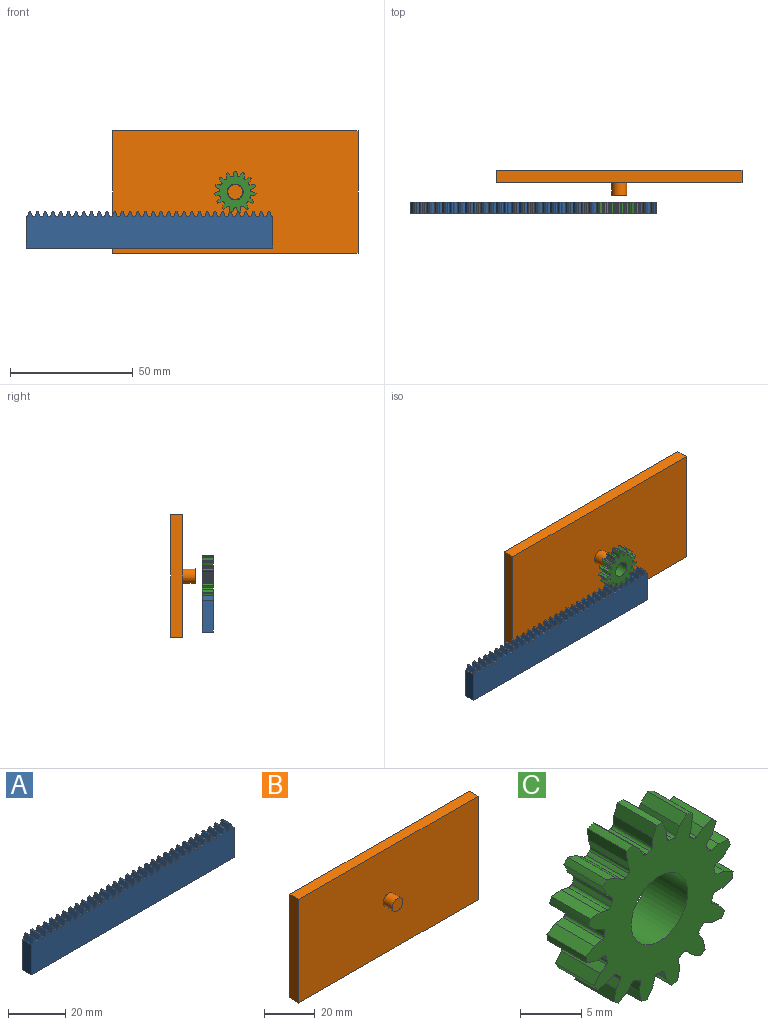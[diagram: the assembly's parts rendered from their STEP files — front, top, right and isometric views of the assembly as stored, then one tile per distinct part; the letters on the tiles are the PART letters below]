
ASSEMBLY  parts=3 mates=2
PART A: 134 faces, bbox 100.5x4.5x15 mm
  f0: plane 4.5x0.53mm, normal (0,0,1), area 2.4mm2, adj f1,f131,f132,f133
  f1: plane 4.5x2.1mm, normal (0.94,0,0.34), area 10.1mm2, adj f0,f2,f132,f133
  f2: plane 4.5x0.55mm, normal (0,0,1), area 2.5mm2, adj f1,f3,f132,f133
  f3: plane 4.5x2.1mm, normal (-0.94,0,0.34), area 10.1mm2, adj f2,f4,f132,f133
  f4: plane 4.5x1.07mm, normal (0,0,1), area 4.8mm2, adj f3,f5,f132,f133
  f5: plane 4.5x2.1mm, normal (0.94,0,0.34), area 10.1mm2, adj f4,f6,f132,f133
  f6: plane 4.5x0.55mm, normal (0,0,1), area 2.5mm2, adj f5,f7,f132,f133
  f7: plane 4.5x2.1mm, normal (-0.94,0,0.34), area 10.1mm2, adj f6,f8,f132,f133
  f8: plane 4.5x1.07mm, normal (0,0,1), area 4.8mm2, adj f7,f9,f132,f133
  f9: plane 4.5x2.1mm, normal (0.94,0,0.34), area 10.1mm2, adj f8,f10,f132,f133
  f10: plane 4.5x0.55mm, normal (0,0,1), area 2.5mm2, adj f9,f11,f132,f133
  f11: plane 4.5x2.1mm, normal (-0.94,0,0.34), area 10.1mm2, adj f10,f12,f132,f133
  f12: plane 4.5x1.07mm, normal (0,0,1), area 4.8mm2, adj f11,f13,f132,f133
  f13: plane 4.5x2.1mm, normal (0.94,0,0.34), area 10.1mm2, adj f12,f14,f132,f133
  f14: plane 4.5x0.55mm, normal (0,0,1), area 2.5mm2, adj f13,f15,f132,f133
  f15: plane 4.5x2.1mm, normal (-0.94,0,0.34), area 10.1mm2, adj f14,f16,f132,f133
  f16: plane 4.5x1.07mm, normal (0,0,1), area 4.8mm2, adj f15,f17,f132,f133
  f17: plane 4.5x2.1mm, normal (0.94,0,0.34), area 10.1mm2, adj f16,f18,f132,f133
  f18: plane 4.5x0.55mm, normal (0,0,1), area 2.5mm2, adj f17,f19,f132,f133
  f19: plane 4.5x2.1mm, normal (-0.94,0,0.34), area 10.1mm2, adj f18,f20,f132,f133
  f20: plane 4.5x1.07mm, normal (0,0,1), area 4.8mm2, adj f19,f21,f132,f133
  f21: plane 4.5x2.1mm, normal (0.94,0,0.34), area 10.1mm2, adj f20,f22,f132,f133
  f22: plane 4.5x0.55mm, normal (0,0,1), area 2.5mm2, adj f21,f23,f132,f133
  f23: plane 4.5x2.1mm, normal (-0.94,0,0.34), area 10.1mm2, adj f22,f24,f132,f133
  f24: plane 4.5x1.07mm, normal (0,0,1), area 4.8mm2, adj f23,f25,f132,f133
  f25: plane 4.5x2.1mm, normal (0.94,0,0.34), area 10.1mm2, adj f24,f26,f132,f133
  f26: plane 4.5x0.55mm, normal (0,0,1), area 2.5mm2, adj f25,f27,f132,f133
  f27: plane 4.5x2.1mm, normal (-0.94,0,0.34), area 10.1mm2, adj f26,f28,f132,f133
  f28: plane 4.5x1.07mm, normal (0,0,1), area 4.8mm2, adj f27,f29,f132,f133
  f29: plane 4.5x2.1mm, normal (0.94,0,0.34), area 10.1mm2, adj f28,f30,f132,f133
  f30: plane 4.5x0.55mm, normal (0,0,1), area 2.5mm2, adj f29,f31,f132,f133
  f31: plane 4.5x2.1mm, normal (-0.94,0,0.34), area 10.1mm2, adj f30,f32,f132,f133
  f32: plane 4.5x1.07mm, normal (0,0,1), area 4.8mm2, adj f31,f33,f132,f133
  f33: plane 4.5x2.1mm, normal (0.94,0,0.34), area 10.1mm2, adj f32,f34,f132,f133
  f34: plane 4.5x0.55mm, normal (0,0,1), area 2.5mm2, adj f33,f35,f132,f133
  f35: plane 4.5x2.1mm, normal (-0.94,0,0.34), area 10.1mm2, adj f34,f36,f132,f133
  f36: plane 4.5x1.07mm, normal (0,0,1), area 4.8mm2, adj f35,f37,f132,f133
  f37: plane 4.5x2.1mm, normal (0.94,0,0.34), area 10.1mm2, adj f36,f38,f132,f133
  f38: plane 4.5x0.55mm, normal (0,0,1), area 2.5mm2, adj f37,f39,f132,f133
  f39: plane 4.5x2.1mm, normal (-0.94,0,0.34), area 10.1mm2, adj f38,f40,f132,f133
  f40: plane 4.5x1.07mm, normal (0,0,1), area 4.8mm2, adj f39,f41,f132,f133
  f41: plane 4.5x2.1mm, normal (0.94,0,0.34), area 10.1mm2, adj f40,f42,f132,f133
  f42: plane 4.5x0.55mm, normal (0,0,1), area 2.5mm2, adj f41,f43,f132,f133
  f43: plane 4.5x2.1mm, normal (-0.94,0,0.34), area 10.1mm2, adj f42,f44,f132,f133
  f44: plane 4.5x1.07mm, normal (0,0,1), area 4.8mm2, adj f43,f45,f132,f133
  f45: plane 4.5x2.1mm, normal (0.94,0,0.34), area 10.1mm2, adj f44,f46,f132,f133
  f46: plane 4.5x0.55mm, normal (0,0,1), area 2.5mm2, adj f45,f47,f132,f133
  f47: plane 4.5x2.1mm, normal (-0.94,0,0.34), area 10.1mm2, adj f46,f48,f132,f133
  f48: plane 4.5x1.07mm, normal (0,0,1), area 4.8mm2, adj f47,f49,f132,f133
  f49: plane 4.5x2.1mm, normal (0.94,0,0.34), area 10.1mm2, adj f48,f50,f132,f133
  f50: plane 4.5x0.55mm, normal (0,0,1), area 2.5mm2, adj f49,f51,f132,f133
  f51: plane 4.5x2.1mm, normal (-0.94,0,0.34), area 10.1mm2, adj f50,f52,f132,f133
  f52: plane 4.5x1.07mm, normal (0,0,1), area 4.8mm2, adj f51,f53,f132,f133
  f53: plane 4.5x2.1mm, normal (0.94,0,0.34), area 10.1mm2, adj f52,f54,f132,f133
  f54: plane 4.5x0.55mm, normal (0,0,1), area 2.5mm2, adj f53,f55,f132,f133
  f55: plane 4.5x2.1mm, normal (-0.94,0,0.34), area 10.1mm2, adj f54,f56,f132,f133
  f56: plane 4.5x1.07mm, normal (0,0,1), area 4.8mm2, adj f55,f57,f132,f133
  f57: plane 4.5x2.1mm, normal (0.94,0,0.34), area 10.1mm2, adj f56,f58,f132,f133
  f58: plane 4.5x0.55mm, normal (0,0,1), area 2.5mm2, adj f57,f59,f132,f133
  f59: plane 4.5x2.1mm, normal (-0.94,0,0.34), area 10.1mm2, adj f58,f60,f132,f133
  f60: plane 4.5x1.07mm, normal (0,0,1), area 4.8mm2, adj f59,f61,f132,f133
  f61: plane 4.5x2.1mm, normal (0.94,0,0.34), area 10.1mm2, adj f60,f62,f132,f133
  f62: plane 4.5x0.55mm, normal (0,0,1), area 2.5mm2, adj f61,f63,f132,f133
  f63: plane 4.5x2.1mm, normal (-0.94,0,0.34), area 10.1mm2, adj f62,f64,f132,f133
  f64: plane 4.5x1.07mm, normal (0,0,1), area 4.8mm2, adj f63,f65,f132,f133
  f65: plane 4.5x2.1mm, normal (0.94,0,0.34), area 10.1mm2, adj f64,f66,f132,f133
  f66: plane 4.5x0.55mm, normal (0,0,1), area 2.5mm2, adj f65,f67,f132,f133
  f67: plane 4.5x2.1mm, normal (-0.94,0,0.34), area 10.1mm2, adj f66,f68,f132,f133
  f68: plane 4.5x1.07mm, normal (0,0,1), area 4.8mm2, adj f67,f69,f132,f133
  f69: plane 4.5x2.1mm, normal (0.94,0,0.34), area 10.1mm2, adj f68,f70,f132,f133
  f70: plane 4.5x0.55mm, normal (0,0,1), area 2.5mm2, adj f69,f71,f132,f133
  f71: plane 4.5x2.1mm, normal (-0.94,0,0.34), area 10.1mm2, adj f70,f72,f132,f133
  f72: plane 4.5x1.07mm, normal (0,0,1), area 4.8mm2, adj f71,f73,f132,f133
  f73: plane 4.5x2.1mm, normal (0.94,0,0.34), area 10.1mm2, adj f72,f74,f132,f133
  f74: plane 4.5x0.55mm, normal (0,0,1), area 2.5mm2, adj f73,f75,f132,f133
  f75: plane 4.5x2.1mm, normal (-0.94,0,0.34), area 10.1mm2, adj f74,f76,f132,f133
  f76: plane 4.5x1.07mm, normal (0,0,1), area 4.8mm2, adj f75,f77,f132,f133
  f77: plane 4.5x2.1mm, normal (0.94,0,0.34), area 10.1mm2, adj f76,f78,f132,f133
  f78: plane 4.5x0.55mm, normal (0,0,1), area 2.5mm2, adj f77,f79,f132,f133
  f79: plane 4.5x2.1mm, normal (-0.94,0,0.34), area 10.1mm2, adj f78,f80,f132,f133
  f80: plane 4.5x1.07mm, normal (0,0,1), area 4.8mm2, adj f79,f81,f132,f133
  f81: plane 4.5x2.1mm, normal (0.94,0,0.34), area 10.1mm2, adj f80,f82,f132,f133
  f82: plane 4.5x0.55mm, normal (0,0,1), area 2.5mm2, adj f81,f83,f132,f133
  f83: plane 4.5x2.1mm, normal (-0.94,0,0.34), area 10.1mm2, adj f82,f84,f132,f133
  f84: plane 4.5x1.07mm, normal (0,0,1), area 4.8mm2, adj f83,f85,f132,f133
  f85: plane 4.5x2.1mm, normal (0.94,0,0.34), area 10.1mm2, adj f84,f86,f132,f133
  f86: plane 4.5x0.55mm, normal (0,0,1), area 2.5mm2, adj f85,f87,f132,f133
  f87: plane 4.5x2.1mm, normal (-0.94,0,0.34), area 10.1mm2, adj f86,f88,f132,f133
  f88: plane 4.5x1.07mm, normal (0,0,1), area 4.8mm2, adj f87,f89,f132,f133
  f89: plane 4.5x2.1mm, normal (0.94,0,0.34), area 10.1mm2, adj f88,f90,f132,f133
  f90: plane 4.5x0.55mm, normal (0,0,1), area 2.5mm2, adj f89,f91,f132,f133
  f91: plane 4.5x2.1mm, normal (-0.94,0,0.34), area 10.1mm2, adj f90,f92,f132,f133
  f92: plane 4.5x1.07mm, normal (0,0,1), area 4.8mm2, adj f91,f93,f132,f133
  f93: plane 4.5x2.1mm, normal (0.94,0,0.34), area 10.1mm2, adj f92,f94,f132,f133
  f94: plane 4.5x0.55mm, normal (0,0,1), area 2.5mm2, adj f93,f95,f132,f133
  f95: plane 4.5x2.1mm, normal (-0.94,0,0.34), area 10.1mm2, adj f94,f96,f132,f133
  f96: plane 4.5x1.07mm, normal (0,0,1), area 4.8mm2, adj f95,f97,f132,f133
  f97: plane 4.5x2.1mm, normal (0.94,0,0.34), area 10.1mm2, adj f96,f98,f132,f133
  f98: plane 4.5x0.55mm, normal (0,0,1), area 2.5mm2, adj f97,f99,f132,f133
  f99: plane 4.5x2.1mm, normal (-0.94,0,0.34), area 10.1mm2, adj f98,f100,f132,f133
  f100: plane 4.5x1.07mm, normal (0,0,1), area 4.8mm2, adj f99,f101,f132,f133
  f101: plane 4.5x2.1mm, normal (0.94,0,0.34), area 10.1mm2, adj f100,f102,f132,f133
  f102: plane 4.5x0.55mm, normal (0,0,1), area 2.5mm2, adj f101,f103,f132,f133
  f103: plane 4.5x2.1mm, normal (-0.94,0,0.34), area 10.1mm2, adj f102,f104,f132,f133
  f104: plane 4.5x1.07mm, normal (0,0,1), area 4.8mm2, adj f103,f105,f132,f133
  f105: plane 4.5x2.1mm, normal (0.94,0,0.34), area 10.1mm2, adj f104,f106,f132,f133
  f106: plane 4.5x0.55mm, normal (0,0,1), area 2.5mm2, adj f105,f107,f132,f133
  f107: plane 4.5x2.1mm, normal (-0.94,0,0.34), area 10.1mm2, adj f106,f108,f132,f133
  f108: plane 4.5x1.07mm, normal (0,0,1), area 4.8mm2, adj f107,f109,f132,f133
  f109: plane 4.5x2.1mm, normal (0.94,0,0.34), area 10.1mm2, adj f108,f110,f132,f133
  f110: plane 4.5x0.55mm, normal (0,0,1), area 2.5mm2, adj f109,f111,f132,f133
  f111: plane 4.5x2.1mm, normal (-0.94,0,0.34), area 10.1mm2, adj f110,f112,f132,f133
  f112: plane 4.5x1.07mm, normal (0,0,1), area 4.8mm2, adj f111,f113,f132,f133
  f113: plane 4.5x2.1mm, normal (0.94,0,0.34), area 10.1mm2, adj f112,f114,f132,f133
  f114: plane 4.5x0.55mm, normal (0,0,1), area 2.5mm2, adj f113,f115,f132,f133
  f115: plane 4.5x2.1mm, normal (-0.94,0,0.34), area 10.1mm2, adj f114,f116,f132,f133
  f116: plane 4.5x1.07mm, normal (0,0,1), area 4.8mm2, adj f115,f117,f132,f133
  f117: plane 4.5x2.1mm, normal (0.94,0,0.34), area 10.1mm2, adj f116,f118,f132,f133
  f118: plane 4.5x0.55mm, normal (0,0,1), area 2.5mm2, adj f117,f119,f132,f133
  f119: plane 4.5x2.1mm, normal (-0.94,0,0.34), area 10.1mm2, adj f118,f120,f132,f133
  f120: plane 4.5x1.07mm, normal (0,0,1), area 4.8mm2, adj f119,f121,f132,f133
  f121: plane 4.5x2.1mm, normal (0.94,0,0.34), area 10.1mm2, adj f120,f122,f132,f133
  f122: plane 4.5x0.55mm, normal (0,0,1), area 2.5mm2, adj f121,f123,f132,f133
  f123: plane 4.5x2.1mm, normal (-0.94,0,0.34), area 10.1mm2, adj f122,f124,f132,f133
  f124: plane 4.5x1.07mm, normal (0,0,1), area 4.8mm2, adj f123,f125,f132,f133
  f125: plane 4.5x2.1mm, normal (0.94,0,0.34), area 10.1mm2, adj f124,f126,f132,f133
  f126: plane 4.5x0.55mm, normal (0,0,1), area 2.5mm2, adj f125,f127,f132,f133
  f127: plane 4.5x2.1mm, normal (-0.94,0,0.34), area 10.1mm2, adj f126,f128,f132,f133
  f128: plane 4.5x0.53mm, normal (0,0,1), area 2.4mm2, adj f127,f129,f132,f133
  f129: plane 12.9x4.5mm, normal (-1,0,0), area 58mm2, adj f128,f130,f132,f133
  f130: plane 100.54x4.5mm, normal (0,0,-1), area 452.4mm2, adj f129,f131,f132,f133
  f131: plane 12.9x4.5mm, normal (1,0,0), area 58mm2, adj f0,f130,f132,f133
  f132: plane 100.54x15mm, normal (0,-1,0), area 1385.1mm2, adj f0,f1,f2,f3,f4,f5,f6,f7
  f133: plane 100.54x15mm, normal (0,1,0), area 1385.1mm2, adj f0,f1,f2,f3,f4,f5,f6,f7
PART B: 8 faces, bbox 100x10x50 mm
  f0: plane 100x5mm, normal (0,0,1), area 500mm2, adj f1,f3,f4,f5
  f1: plane 50x5mm, normal (-1,0,0), area 250mm2, adj f0,f2,f4,f5
  f2: plane 100x5mm, normal (0,0,-1), area 500mm2, adj f1,f3,f4,f5
  f3: plane 50x5mm, normal (1,0,0), area 250mm2, adj f0,f2,f4,f5
  f4: plane 100x50mm, normal (0,-1,0), area 4971.7mm2, adj f0,f1,f2,f3,f6
  f5: plane 100x50mm, normal (0,1,0), area 5000mm2, adj f0,f1,f2,f3
  f6: cylinder r=3mm len=6mm, axis (0,1,0), area 94.2mm2, adj f4,f7
  f7: plane 6x6mm, normal (0,-1,0), area 28.3mm2, adj f6
PART C: 123 faces, bbox 17x4.5x16.9 mm
  f0: cylinder r=0.3mm len=4.5mm, axis (0,1,0), area 1.8mm2, adj f1,f120,f121,f122
  f1: plane 4.5x0.88mm, normal (-0.2,0,0.98), area 4mm2, adj f0,f2,f121,f122
  f2: plane 4.5x0.98mm, normal (-0.49,0,0.87), area 5.1mm2, adj f1,f3,f121,f122
  f3: cylinder r=8.5mm len=4.5mm, axis (0,1,0), area 3mm2, adj f2,f4,f121,f122
  f4: plane 4.5x1.07mm, normal (-0.29,0,-0.96), area 5.1mm2, adj f3,f5,f121,f122
  f5: plane 4.5x0.89mm, normal (0.01,0,-1), area 4mm2, adj f4,f6,f121,f122
  f6: cylinder r=0.3mm len=4.5mm, axis (0,1,0), area 1.8mm2, adj f5,f7,f121,f122
  f7: cylinder r=6.4mm len=4.5mm, axis (0,1,0), area 2.1mm2, adj f6,f8,f121,f122
  f8: cylinder r=0.3mm len=4.5mm, axis (0,1,0), area 1.8mm2, adj f7,f9,f121,f122
  f9: plane 4.5x0.73mm, normal (-0.58,0,0.82), area 4mm2, adj f8,f10,f121,f122
  f10: plane 4.5x0.9mm, normal (-0.8,0,0.6), area 5.1mm2, adj f9,f11,f121,f122
  f11: cylinder r=8.5mm len=4.5mm, axis (0,1,0), area 3mm2, adj f10,f12,f121,f122
  f12: plane 4.5x1.12mm, normal (0.12,0,-0.99), area 5.1mm2, adj f11,f13,f121,f122
  f13: plane 4.5x0.81mm, normal (0.42,0,-0.91), area 4mm2, adj f12,f14,f121,f122
  f14: cylinder r=0.3mm len=4.5mm, axis (0,1,0), area 1.8mm2, adj f13,f15,f121,f122
  f15: cylinder r=6.4mm len=4.5mm, axis (0,1,0), area 2.1mm2, adj f14,f16,f121,f122
  f16: cylinder r=0.3mm len=4.5mm, axis (0,1,0), area 1.8mm2, adj f15,f17,f121,f122
  f17: plane 4.5x0.77mm, normal (-0.86,0,0.51), area 4mm2, adj f16,f18,f121,f122
  f18: plane 4.5x1.1mm, normal (-0.97,0,0.22), area 5.1mm2, adj f17,f19,f121,f122
  f19: cylinder r=8.5mm len=4.5mm, axis (0,1,0), area 3mm2, adj f18,f20,f121,f122
  f20: plane 4.5x0.96mm, normal (0.51,0,-0.86), area 5.1mm2, adj f19,f21,f121,f122
  f21: plane 4.5x0.67mm, normal (0.75,0,-0.66), area 4mm2, adj f20,f22,f121,f122
  f22: cylinder r=0.3mm len=4.5mm, axis (0,1,0), area 1.8mm2, adj f21,f23,f121,f122
  f23: cylinder r=6.4mm len=4.5mm, axis (0,1,0), area 2.1mm2, adj f22,f24,f121,f122
  f24: cylinder r=0.3mm len=4.5mm, axis (0,1,0), area 1.8mm2, adj f23,f25,f121,f122
  f25: plane 4.5x0.89mm, normal (-0.99,0,0.12), area 4mm2, adj f24,f26,f121,f122
  f26: plane 4.5x1.1mm, normal (-0.98,0,-0.19), area 5.1mm2, adj f25,f27,f121,f122
  f27: cylinder r=8.5mm len=4.5mm, axis (0,1,0), area 3mm2, adj f26,f28,f121,f122
  f28: plane 4.5x0.92mm, normal (0.82,0,-0.58), area 5.1mm2, adj f27,f29,f121,f122
  f29: plane 4.5x0.85mm, normal (0.95,0,-0.3), area 4mm2, adj f28,f30,f121,f122
  f30: cylinder r=0.3mm len=4.5mm, axis (0,1,0), area 1.8mm2, adj f29,f31,f121,f122
  f31: cylinder r=6.4mm len=4.5mm, axis (0,1,0), area 2.1mm2, adj f30,f32,f121,f122
  f32: cylinder r=0.3mm len=4.5mm, axis (0,1,0), area 1.8mm2, adj f31,f33,f121,f122
  f33: plane 4.5x0.85mm, normal (-0.95,0,-0.3), area 4mm2, adj f32,f34,f121,f122
  f34: plane 4.5x0.92mm, normal (-0.82,0,-0.58), area 5.1mm2, adj f33,f35,f121,f122
  f35: cylinder r=8.5mm len=4.5mm, axis (0,1,0), area 3mm2, adj f34,f36,f121,f122
  f36: plane 4.5x1.1mm, normal (0.98,0,-0.19), area 5.1mm2, adj f35,f37,f121,f122
  f37: plane 4.5x0.89mm, normal (0.99,0,0.12), area 4mm2, adj f36,f38,f121,f122
  f38: cylinder r=0.3mm len=4.5mm, axis (0,1,0), area 1.8mm2, adj f37,f39,f121,f122
  f39: cylinder r=6.4mm len=4.5mm, axis (0,1,0), area 2.1mm2, adj f38,f40,f121,f122
  f40: cylinder r=0.3mm len=4.5mm, axis (0,1,0), area 1.8mm2, adj f39,f41,f121,f122
  f41: plane 4.5x0.67mm, normal (-0.75,0,-0.66), area 4mm2, adj f40,f42,f121,f122
  f42: plane 4.5x0.96mm, normal (-0.51,0,-0.86), area 5.1mm2, adj f41,f43,f121,f122
  f43: cylinder r=8.5mm len=4.5mm, axis (0,1,0), area 3mm2, adj f42,f44,f121,f122
  f44: plane 4.5x1.1mm, normal (0.97,0,0.22), area 5.1mm2, adj f43,f45,f121,f122
  f45: plane 4.5x0.77mm, normal (0.86,0,0.51), area 4mm2, adj f44,f46,f121,f122
  f46: cylinder r=0.3mm len=4.5mm, axis (0,1,0), area 1.8mm2, adj f45,f47,f121,f122
  f47: cylinder r=6.4mm len=4.5mm, axis (0,1,0), area 2.1mm2, adj f46,f48,f121,f122
  f48: cylinder r=0.3mm len=4.5mm, axis (0,1,0), area 1.8mm2, adj f47,f49,f121,f122
  f49: plane 4.5x0.81mm, normal (-0.42,0,-0.91), area 4mm2, adj f48,f50,f121,f122
  f50: plane 4.5x1.12mm, normal (-0.12,0,-0.99), area 5.1mm2, adj f49,f51,f121,f122
  f51: cylinder r=8.5mm len=4.5mm, axis (0,1,0), area 3mm2, adj f50,f52,f121,f122
  f52: plane 4.5x0.9mm, normal (0.8,0,0.6), area 5.1mm2, adj f51,f53,f121,f122
  f53: plane 4.5x0.73mm, normal (0.58,0,0.82), area 4mm2, adj f52,f54,f121,f122
  f54: cylinder r=0.3mm len=4.5mm, axis (0,1,0), area 1.8mm2, adj f53,f55,f121,f122
  f55: cylinder r=6.4mm len=4.5mm, axis (0,1,0), area 2.1mm2, adj f54,f56,f121,f122
  f56: cylinder r=0.3mm len=4.5mm, axis (0,1,0), area 1.8mm2, adj f55,f57,f121,f122
  f57: plane 4.5x0.89mm, normal (-0.01,0,-1), area 4mm2, adj f56,f58,f121,f122
  f58: plane 4.5x1.07mm, normal (0.29,0,-0.96), area 5.1mm2, adj f57,f59,f121,f122
  f59: cylinder r=8.5mm len=4.5mm, axis (0,1,0), area 3mm2, adj f58,f60,f121,f122
  f60: plane 4.5x0.98mm, normal (0.49,0,0.87), area 5.1mm2, adj f59,f61,f121,f122
  f61: plane 4.5x0.88mm, normal (0.2,0,0.98), area 4mm2, adj f60,f62,f121,f122
  f62: cylinder r=0.3mm len=4.5mm, axis (0,1,0), area 1.8mm2, adj f61,f63,f121,f122
  f63: cylinder r=6.4mm len=4.5mm, axis (0,1,0), area 2.1mm2, adj f62,f64,f121,f122
  f64: cylinder r=0.3mm len=4.5mm, axis (0,1,0), area 1.8mm2, adj f63,f65,f121,f122
  f65: plane 4.5x0.82mm, normal (0.4,0,-0.92), area 4mm2, adj f64,f66,f121,f122
  f66: plane 4.5x0.85mm, normal (0.66,0,-0.75), area 5.1mm2, adj f65,f67,f121,f122
  f67: cylinder r=8.5mm len=4.5mm, axis (0,1,0), area 3mm2, adj f66,f68,f121,f122
  f68: plane 4.5x1.12mm, normal (0.09,0,1), area 5.1mm2, adj f67,f69,f121,f122
  f69: plane 4.5x0.87mm, normal (-0.22,0,0.98), area 4mm2, adj f68,f70,f121,f122
  f70: cylinder r=0.3mm len=4.5mm, axis (0,1,0), area 1.8mm2, adj f69,f71,f121,f122
  f71: cylinder r=6.4mm len=4.5mm, axis (0,1,0), area 2.1mm2, adj f70,f72,f121,f122
  f72: cylinder r=0.3mm len=4.5mm, axis (0,1,0), area 1.8mm2, adj f71,f73,f121,f122
  f73: plane 4.5x0.66mm, normal (0.74,0,-0.68), area 4mm2, adj f72,f74,f121,f122
  f74: plane 4.5x1.02mm, normal (0.91,0,-0.42), area 5.1mm2, adj f73,f75,f121,f122
  f75: cylinder r=8.5mm len=4.5mm, axis (0,1,0), area 3mm2, adj f74,f76,f121,f122
  f76: plane 4.5x1.06mm, normal (-0.32,0,0.95), area 5.1mm2, adj f75,f77,f121,f122
  f77: plane 4.5x0.72mm, normal (-0.6,0,0.8), area 4mm2, adj f76,f78,f121,f122
  f78: cylinder r=0.3mm len=4.5mm, axis (0,1,0), area 1.8mm2, adj f77,f79,f121,f122
  f79: cylinder r=6.4mm len=4.5mm, axis (0,1,0), area 2.1mm2, adj f78,f80,f121,f122
  f80: cylinder r=0.3mm len=4.5mm, axis (0,1,0), area 1.8mm2, adj f79,f81,f121,f122
  f81: plane 4.5x0.85mm, normal (0.95,0,-0.32), area 4mm2, adj f80,f82,f121,f122
  f82: plane 4.5x1.12mm, normal (1,0,-0.02), area 5.1mm2, adj f81,f83,f121,f122
  f83: cylinder r=8.5mm len=4.5mm, axis (0,1,0), area 3mm2, adj f82,f84,f121,f122
  f84: plane 4.5x0.82mm, normal (-0.68,0,0.73), area 5.1mm2, adj f83,f85,f121,f122
  f85: plane 4.5x0.78mm, normal (-0.87,0,0.49), area 4mm2, adj f84,f86,f121,f122
  f86: cylinder r=0.3mm len=4.5mm, axis (0,1,0), area 1.8mm2, adj f85,f87,f121,f122
  f87: cylinder r=6.4mm len=4.5mm, axis (0,1,0), area 2.1mm2, adj f86,f88,f121,f122
  f88: cylinder r=0.3mm len=4.5mm, axis (0,1,0), area 1.8mm2, adj f87,f89,f121,f122
  f89: plane 4.5x0.89mm, normal (1,0,0.09), area 4mm2, adj f88,f90,f121,f122
  f90: plane 4.5x1.03mm, normal (0.92,0,0.39), area 5.1mm2, adj f89,f91,f121,f122
  f91: cylinder r=8.5mm len=4.5mm, axis (0,1,0), area 3mm2, adj f90,f92,f121,f122
  f92: plane 4.5x1.03mm, normal (-0.92,0,0.39), area 5.1mm2, adj f91,f93,f121,f122
  f93: plane 4.5x0.89mm, normal (-1,0,0.09), area 4mm2, adj f92,f94,f121,f122
  f94: cylinder r=0.3mm len=4.5mm, axis (0,1,0), area 1.8mm2, adj f93,f95,f121,f122
  f95: cylinder r=6.4mm len=4.5mm, axis (0,1,0), area 2.1mm2, adj f94,f96,f121,f122
  f96: cylinder r=0.3mm len=4.5mm, axis (0,1,0), area 1.8mm2, adj f95,f97,f121,f122
  f97: plane 4.5x0.78mm, normal (0.87,0,0.49), area 4mm2, adj f96,f98,f121,f122
  f98: plane 4.5x0.82mm, normal (0.68,0,0.73), area 5.1mm2, adj f97,f99,f121,f122
  f99: cylinder r=8.5mm len=4.5mm, axis (0,1,0), area 3mm2, adj f98,f100,f121,f122
  f100: plane 4.5x1.12mm, normal (-1,0,-0.02), area 5.1mm2, adj f99,f101,f121,f122
  f101: plane 4.5x0.85mm, normal (-0.95,0,-0.32), area 4mm2, adj f100,f102,f121,f122
  f102: cylinder r=0.3mm len=4.5mm, axis (0,1,0), area 1.8mm2, adj f101,f103,f121,f122
  f103: cylinder r=6.4mm len=4.5mm, axis (0,1,0), area 2.1mm2, adj f102,f104,f121,f122
  f104: cylinder r=0.3mm len=4.5mm, axis (0,1,0), area 1.8mm2, adj f103,f105,f121,f122
  f105: plane 4.5x0.72mm, normal (0.6,0,0.8), area 4mm2, adj f104,f106,f121,f122
  f106: plane 4.5x1.06mm, normal (0.32,0,0.95), area 5.1mm2, adj f105,f107,f121,f122
  f107: cylinder r=8.5mm len=4.5mm, axis (0,1,0), area 3mm2, adj f106,f108,f121,f122
  f108: plane 4.5x1.02mm, normal (-0.91,0,-0.42), area 5.1mm2, adj f107,f109,f121,f122
  f109: plane 4.5x0.66mm, normal (-0.74,0,-0.68), area 4mm2, adj f108,f110,f121,f122
  f110: cylinder r=0.3mm len=4.5mm, axis (0,1,0), area 1.8mm2, adj f109,f111,f121,f122
  f111: cylinder r=6.4mm len=4.5mm, axis (0,1,0), area 2.1mm2, adj f110,f112,f121,f122
  f112: cylinder r=0.3mm len=4.5mm, axis (0,1,0), area 1.8mm2, adj f111,f113,f121,f122
  f113: plane 4.5x0.87mm, normal (0.22,0,0.98), area 4mm2, adj f112,f114,f121,f122
  f114: plane 4.5x1.12mm, normal (-0.09,0,1), area 5.1mm2, adj f113,f115,f121,f122
  f115: cylinder r=8.5mm len=4.5mm, axis (0,1,0), area 3mm2, adj f114,f116,f121,f122
  f116: plane 4.5x0.85mm, normal (-0.66,0,-0.75), area 5.1mm2, adj f115,f117,f121,f122
  f117: plane 4.5x0.82mm, normal (-0.4,0,-0.92), area 4mm2, adj f116,f118,f121,f122
  f118: cylinder r=0.3mm len=4.5mm, axis (0,1,0), area 1.8mm2, adj f117,f120,f121,f122
  f119: cylinder r=3.25mm len=6.5mm, axis (0,1,0), area 91.9mm2, adj f121,f122
  f120: cylinder r=6.4mm len=4.5mm, axis (0,1,0), area 2.1mm2, adj f0,f118,f121,f122
  f121: plane 16.96x16.88mm, normal (0,-1,0), area 139.8mm2, adj f0,f1,f2,f3,f4,f5,f6,f7
  f122: plane 16.96x16.88mm, normal (0,1,0), area 139.8mm2, adj f0,f1,f2,f3,f4,f5,f6,f7
PLACE A t=(212.28,12.67,-10.03)mm
PLACE B t=(-197.18,25.65,5.29)mm
PLACE C t=(-197.18,12.67,5.35)mm
MATE cylindrical C.f119 <-> B.f6  axis (0,-1,0) through (-197.18,8.17,5.29)mm
MATE planar A.f132 <-> C.f121  axis (0,-1,0) through (-207.01,8.17,-4.63)mm
